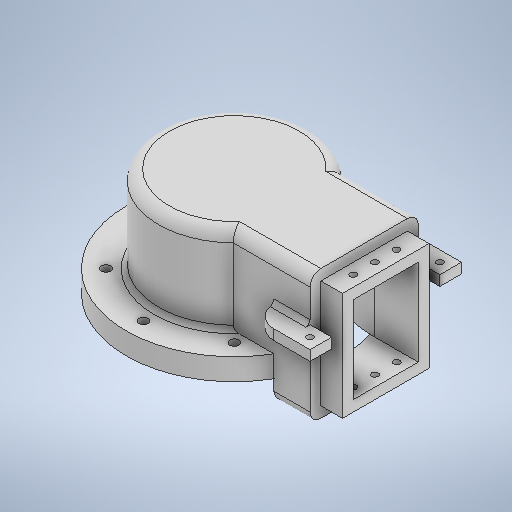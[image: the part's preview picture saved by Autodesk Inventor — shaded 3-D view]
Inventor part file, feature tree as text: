
AUTODESK INVENTOR PART (.ipt)
format: ipt  version: 2025 (Build 290162000, 162)  size: 459,264 bytes
history: native  units: mm
features: sketch x11, extrude x9, fillet x6, plane x1, mirror x1
ambient origin geometry x8: Origin, YZ Plane, XZ Plane, XY Plane, X Axis, Y Axis, Z Axis, Center Point
bodies: Solid1 (feature_tree)
feature tree (28):
  extrude  "Extrusion1"  Depth=100.0mm
  extrude  "Extrusion2"  Depth=42.0mm
  extrude  "Extrusion20"  Depth=10.0mm
  extrude  "Extrusion26"  Depth=70.0mm
  extrude  "Extrusion27"  Depth=30.0mm
  extrude  "Extrusion30"  Depth=10.0mm
  plane  "Work Plane2"
  fillet  "Fillet20"  Radius=10.0mm
  fillet  "Fillet22"  Radius=10.0mm
  fillet  "Fillet23"  Radius=60.0mm
  fillet  "Fillet25"  Radius=10.0mm
  extrude  "Extrusion32"  Depth=100.0mm
  extrude  "Extrusion34"  TaperAngle=0.0deg  [1 undecoded]
  mirror  "Mirror3"
  extrude  "Extrusion35"  Depth=10.0mm TaperAngle=0.0deg
  fillet  "Fillet29"  Radius=10.0mm
  fillet  "Fillet30"  Radius=5.0mm
  sketch  "Sketch1"  dims[d0=60.3mm d1=100.0mm]
  sketch  "Sketch Circular Pattern1"  dims[d3=4.3mm d4=42.0mm]
  sketch  "Sketch2"  dims[d5=80.0mm d7=360.0deg d9=10.0mm]
  sketch  "Sketch25"  dims[d12=60.3mm d13=30.0mm]
  sketch  "Sketch32"  dims[d14=0.0mm d87=25.0mm d88=10.0mm d89=10.0mm d90=60.0mm d91=10.0mm]
  sketch  "Sketch33"  dims[d92=0.0mm d131=100.0mm]
  sketch  "Sketch36"  dims[d132=20.0mm d133=0.0mm]
  sketch  "Sketch38"  dims[d139=10.0mm d140=0.0mm d163=10.0mm d164=0.0mm d176=10.0mm d178=5.0mm]
  sketch  "Sketch Rectangular Pattern5"  dims[d10=0.0mm d11=70.0mm]
  sketch  "Sketch40"  dims[d179=2.0mm]
  sketch  "Sketch41"  dims[d181=2.0mm d188=5.0mm d189=5.0mm d190=5.0mm d191=5.0mm d192=3.0mm d193=10.0mm d194=30.0mm d196=10.0mm d197=10.0mm d199=10.0mm d201=0.0mm d202=0.0mm d205=5.0mm d206=5.0mm d207=5.0mm d208=5.0mm d209=20.0mm d210=4.7mm d211=3.0mm d212=5.0mm d213=5.0mm d214=10.0mm d215=0.0mm d216=0.0mm d217=0.0mm d219=60.0mm d220=5.0mm d2=0.5mm d22=0.5mm d23=0.872665mm d24=0.5mm d25=0.872665mm d31=0.5mm d32=0.872665mm d33=0.5mm d34=0.872665mm d80=0.0mm d81=0.0mm d82=0.0mm d83=0.0mm d84=0.0mm d85=0.0mm d86=0.0mm d134=0.872665mm d170=0.0mm d171=0.0mm d172=0.0mm d173=0.0mm d174=0.0mm d175=0.0mm d177=0.0mm d183=0.5mm d184=0.872665mm d185=0.5mm d186=0.872665mm]
note: 1 required parameter value undecoded (feature->parameter linkage not recoverable at this tier; creation-order binding heuristic only, values carry confidence <= 0.55)
